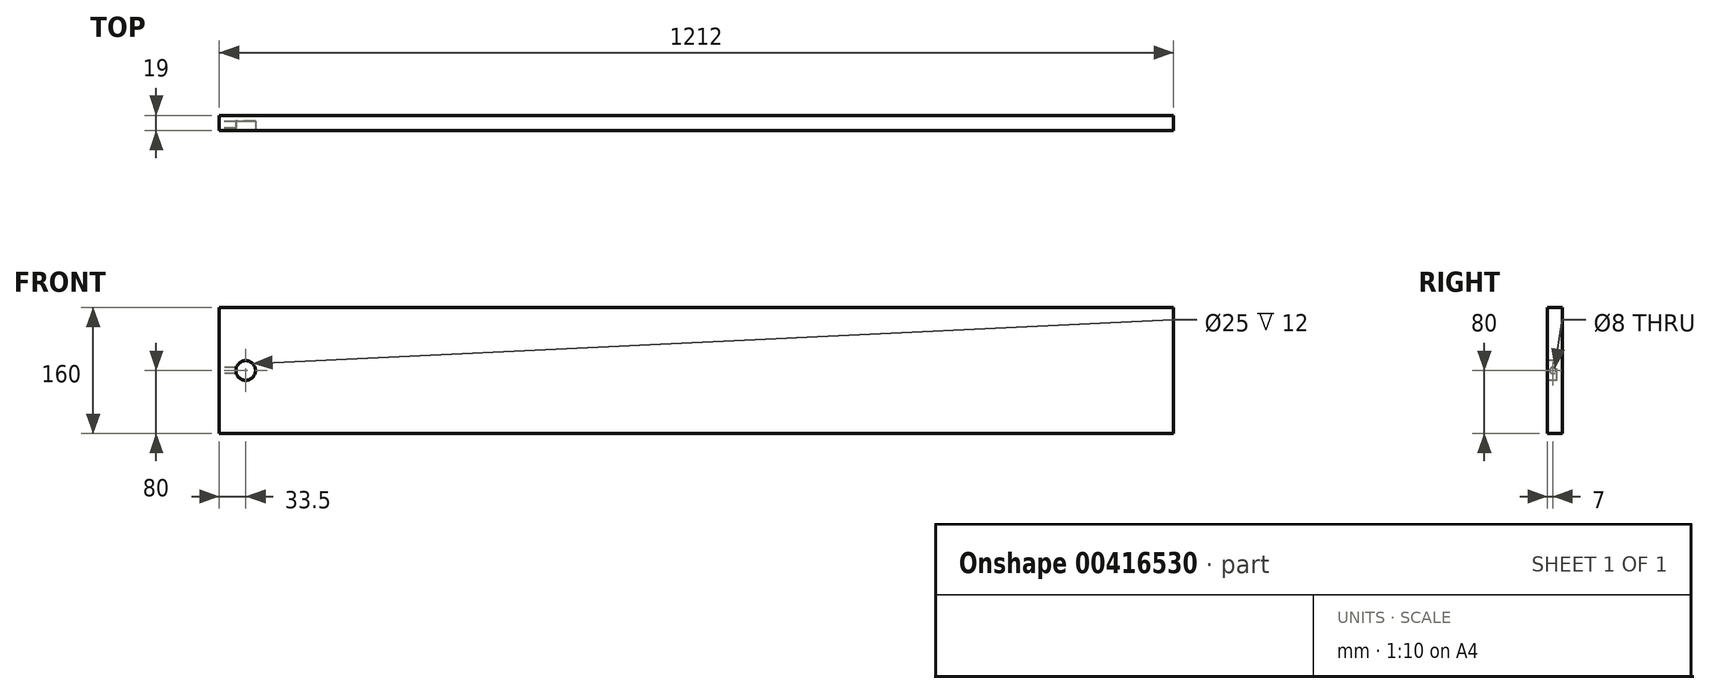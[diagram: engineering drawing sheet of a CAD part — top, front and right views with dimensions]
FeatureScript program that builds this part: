
annotation { "Feature Type Name" : "Feature", "Feature Type Description" : "" }
export const myFeature = defineFeature(function(context is Context, id is Id, definition is map)
    precondition{}
    {
        {
            var Q0;
            Q0=qCreatedBy(makeId("Front.planeOp"),FACE);
            var sketch = newSketch(context, id + "F0", { "sketchPlane" : qUnion([Q0])});
            skLineSegment(sketch, "E0.bottom", {"start": v(-606, -80) * mm, "end": v(606, -80) * mm});
            skLineSegment(sketch, "E0.top", {"start": v(-606, 80) * mm, "end": v(606, 80) * mm});
            skLineSegment(sketch, "E0.left", {"start": v(-606, -80) * mm, "end": v(-606, 80) * mm});
            skLineSegment(sketch, "E0.right", {"start": v(606, -80) * mm, "end": v(606, 80) * mm});
            skPoint(sketch, "E0.middle", {"position": v(0, 0) * mm});
            skSolve(sketch);
        }
        {
            var Q0;
            Q0=makeQuery(id+"F0.imprint","IMPRINT",FACE,{"disambiguationData":[TD([[makeQuery(id+"F0.imprint","IMPRINT",EDGE,{"derivedFrom":sQuery(id+"F0.wireOp",EDGE,"E0.bottom")}),1.0]])]});
            extrude(context, id + "F1", {"entities" : qUnion([Q0]), "depth" : 19 * mm});
        }
        {
            var Q0;
            Q0=makeQuery(id+"F1.opExtrude","CAP_FACE",FACE,{"disambiguationData":[OSD([sQuery(id+"F0.wireOp",EDGE,"E0.bottom"),sQuery(id+"F0.wireOp",EDGE,"E0.top"),sQuery(id+"F0.wireOp",EDGE,"E0.left"),sQuery(id+"F0.wireOp",EDGE,"E0.right")])],"isStart":false});
            var sketch = newSketch(context, id + "F2", { "sketchPlane" : qUnion([Q0])});
            skLineSegment(sketch, "E1", {"start": v(-572.16, 0) * mm, "end": v(-615.32, 0) * mm, "construction": true});
            skPoint(sketch, "E1.startSnap0", {"position": v(-606, 0) * mm});
            skCircle(sketch, "E2", {"center": v(-572.5, 0) * mm, "radius": 12.5 * mm});
            skSolve(sketch);
        }
        {
            var Q0;
            Q0=makeQuery(id+"F2.imprint","IMPRINT",FACE,{"disambiguationData":[TD([[makeQuery(id+"F2.imprint","IMPRINT",EDGE,{"derivedFrom":sQuery(id+"F2.wireOp",EDGE,"E2")}),1.0]])]});
            extrude(context, id + "F3", {"entities" : qUnion([Q0]), "operationType" : NewBodyOperationType.REMOVE, "oppositeDirection" : true, "depth" : 12 * mm});
        }
        {
            var Q0;
            Q0=makeQuery(id+"F1.opExtrude","SWEPT_FACE",FACE,{"disambiguationData":[OSD([sQuery(id+"F0.wireOp",EDGE,"E0.left")])]});
            var sketch = newSketch(context, id + "F4", { "sketchPlane" : qUnion([Q0])});
            skPoint(sketch, "E3", {"position": v(12, 0) * mm});
            skSolve(sketch);
        }
        {
            var Q0;
            Q0=sQuery(id+"F4.wireOp",VERTEX,"E3");
            var Q1;
            Q1=makeQuery(id+"F1.opExtrude","SWEPT_BODY",BODY,{"disambiguationData":[OSD([sQuery(id+"F0.wireOp",EDGE,"E0.bottom"),sQuery(id+"F0.wireOp",EDGE,"E0.top"),sQuery(id+"F0.wireOp",EDGE,"E0.left"),sQuery(id+"F0.wireOp",EDGE,"E0.right")])]});
            hole(context, id + "F5", {"style" : HoleStyle.SIMPLE, "endStyle" : HoleEndStyle.BLIND, "holeDiameter" : 8 * mm, "holeDepth" : 22 * mm, "isTappedThrough" : true, "tappedDepth" : 12 * mm, "tapClearance" : 3, "startFromSketch" : true, "locations" : qUnion([Q0]), "scope" : qUnion([Q1])});
        }
    });
